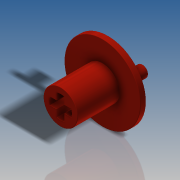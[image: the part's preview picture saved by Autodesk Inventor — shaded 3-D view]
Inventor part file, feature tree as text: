
AUTODESK INVENTOR PART (.ipt)
format: ipt  version: 2016 SP2 (Build 200236200, 236)  size: 182,272 bytes
history: native  units: in
note: dims shown in document units (in); Inventor stores cm internally (conversion verified against a paired STEP export)
features: sketch x3, extrude x2, revolve x1, fillet x1
ambient origin geometry x8: Origin, YZ Plane, XZ Plane, XY Plane, X Axis, Y Axis, Z Axis, Center Point
bodies: Solid1 (feature_tree)
feature tree (7):
  revolve  "Revolution1"  [1 undecoded]
  extrude  "Extrusion1"  Depth=0.3465in
  extrude  "Extrusion2"  Depth=0.0039in
  fillet  "Fillet1"  Radius=0.063in
  sketch  "Sketch2"  dims[d0=0.2835in d1=0.6299in]
  sketch  "Sketch3"  dims[d2=0.0472in d3=0.3465in]
  sketch  "Sketch4"  dims[d4=90.0deg d5=0.189in d6=0.063in d7=0.315in d8=0.0in d9=120.0deg d10=0.0945in d11=0.4409in d12=0.0945in d13=0.0in d14=0.0039in]
note: 1 required parameter value undecoded (feature->parameter linkage not recoverable at this tier; creation-order binding heuristic only, values carry confidence <= 0.55)
